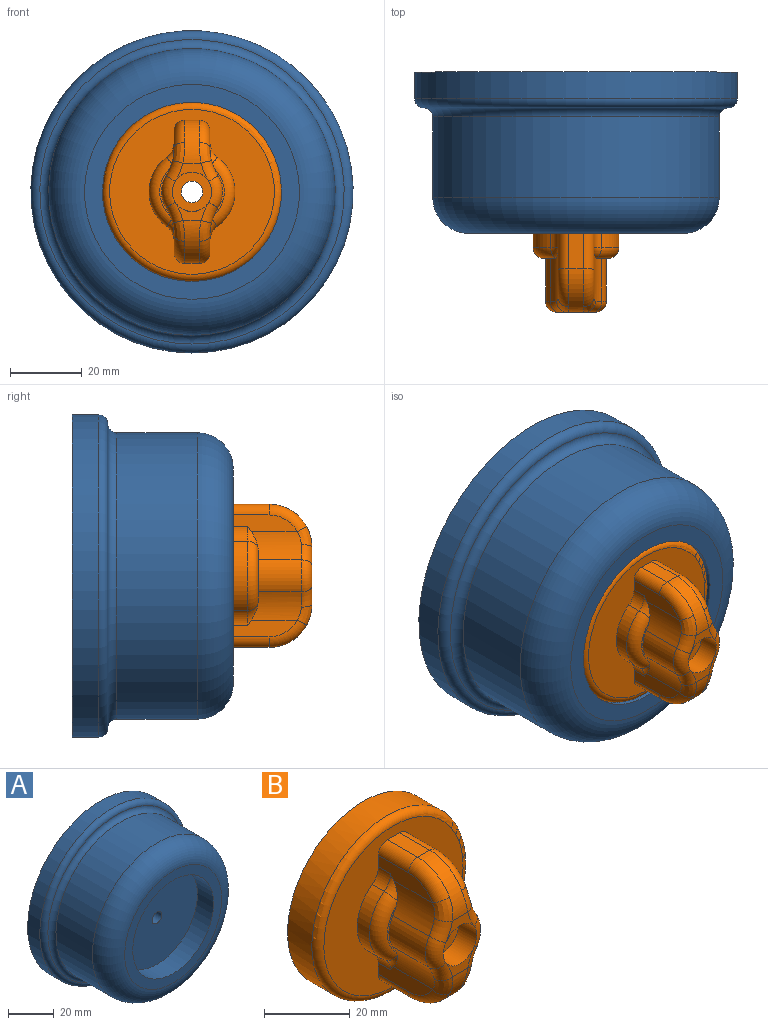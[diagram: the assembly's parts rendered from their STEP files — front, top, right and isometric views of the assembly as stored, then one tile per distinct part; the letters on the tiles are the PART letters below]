
ASSEMBLY  parts=2 mates=1
PART A: 10 faces, bbox 97.4x45x97.4 mm
  f0: cylinder r=3mm len=35mm, axis (0,-1,0), area 659.7mm2, adj f1,f9
  f1: plane 90x90mm, normal (0,1,0), area 6333.5mm2, adj f0,f2
  f2: cylinder r=45mm len=90mm, axis (0,-1,0), area 2120.6mm2, adj f1,f3
  f3: torus R=42.5mm, axis (0,-1,0), area 1087.9mm2, adj f2,f4
  f4: torus R=42.5mm, axis (0,-1,0), area 1009.4mm2, adj f3,f5
  f5: cylinder r=40mm len=80mm, axis (0,-1,0), area 5654.9mm2, adj f4,f6
  f6: torus R=30mm, axis (0,-1,0), area 3589.2mm2, adj f5,f7
  f7: plane 60x60mm, normal (0,-1,0), area 863.9mm2, adj f6,f8
  f8: cylinder r=25mm len=50mm, axis (0,-1,0), area 1570.8mm2, adj f7,f9
  f9: plane 50x50mm, normal (0,-1,0), area 1935.2mm2, adj f0,f8
PART B: 55 faces, bbox 54.1x32.1x54.1 mm
  f0: plane 9.36x5.11mm, normal (0,-1,0), area 18mm2, adj f30,f32,f44,f51
  f1: plane 17.9x4.68mm, normal (-1,0,0), area 66.4mm2, adj f2,f12,f19,f24,f37,f47
  f2: cylinder r=3mm len=10mm, axis (0,1,0), area 47.1mm2, adj f1,f3,f19,f47
  f3: plane 10x4mm, normal (0,0,-1), area 40mm2, adj f2,f4,f19,f33
  f4: cylinder r=3mm len=10mm, axis (0,1,0), area 47.1mm2, adj f3,f5,f19,f40
  f5: plane 17.9x4.68mm, normal (1,0,0), area 66.4mm2, adj f4,f13,f19,f25,f36,f40
  f6: plane 17.9x4.68mm, normal (1,0,0), area 66.4mm2, adj f7,f14,f19,f27,f34,f46
  f7: cylinder r=3mm len=10mm, axis (0,1,0), area 47.1mm2, adj f6,f8,f19,f46
  f8: plane 10x4mm, normal (0,0,1), area 40mm2, adj f7,f9,f19,f32
  f9: cylinder r=3mm len=10mm, axis (0,1,0), area 47.1mm2, adj f8,f10,f19,f53
  f10: plane 17.9x4.68mm, normal (-1,0,0), area 66.4mm2, adj f9,f11,f19,f22,f39,f53
  f11: cylinder r=15mm len=13.94mm, axis (0,1,0), area 101.9mm2, adj f10,f18,f28,f38,f39,f51,f52
  f12: cylinder r=15mm len=13.94mm, axis (0,1,0), area 101.9mm2, adj f1,f18,f28,f37,f38,f48,f49
  f13: cylinder r=15mm len=13.94mm, axis (0,1,0), area 101.9mm2, adj f5,f17,f29,f35,f36,f41,f42
  f14: cylinder r=15mm len=13.94mm, axis (0,1,0), area 101.9mm2, adj f6,f17,f29,f34,f35,f44,f45
  f15: plane 9.36x5.11mm, normal (0,-1,0), area 18mm2, adj f30,f33,f42,f49
  f16: cylinder r=3mm len=26mm, axis (0,-1,0), area 490.1mm2, adj f20,f31
  f17: plane 13.13x2.84mm, normal (0,-1,0), area 6.4mm2, adj f13,f14,f29,f35
  f18: plane 13.13x2.84mm, normal (0,-1,0), area 6.4mm2, adj f11,f12,f28,f38
  f19: plane 46x46mm, normal (0,-1,0), area 1045.5mm2, adj f1,f2,f3,f4,f5,f6,f7,f8
  f20: plane 50x50mm, normal (0,1,0), area 1935.2mm2, adj f16,f21
  f21: cylinder r=25mm len=50mm, axis (0,-1,0), area 1256.6mm2, adj f20,f54
  f22: cylinder r=5mm len=4.04mm, axis (0,1,0), area 18.8mm2, adj f10,f19,f23,f39
  f23: cylinder r=12mm len=19.41mm, axis (0,1,0), area 90.4mm2, adj f19,f22,f24,f38
  f24: cylinder r=5mm len=4.04mm, axis (0,1,0), area 18.8mm2, adj f1,f19,f23,f37
  f25: cylinder r=5mm len=4.04mm, axis (0,1,0), area 18.8mm2, adj f5,f19,f26,f36
  f26: cylinder r=12mm len=19.41mm, axis (0,1,0), area 90.4mm2, adj f19,f25,f27,f35
  f27: cylinder r=5mm len=4.04mm, axis (0,1,0), area 18.8mm2, adj f6,f19,f26,f34
  f28: cylinder r=8.5mm len=12mm, axis (0,1,0), area 112.8mm2, adj f11,f12,f18,f50
  f29: cylinder r=8.5mm len=12mm, axis (0,1,0), area 112.8mm2, adj f13,f14,f17,f43
  f30: cylinder r=5.5mm len=11mm, axis (0,-1,0), area 207.3mm2, adj f0,f15,f31,f43,f50
  f31: plane 11x11mm, normal (0,-1,0), area 66.8mm2, adj f16,f30
  f32: cylinder r=12mm len=12mm, axis (1,0,0), area 77.5mm2, adj f0,f8,f45,f46,f52,f53
  f33: cylinder r=12mm len=12mm, axis (1,0,0), area 77.5mm2, adj f3,f15,f40,f41,f47,f48
  f34: torus R=8mm, axis (0,-1,0), area 9.7mm2, adj f6,f14,f27,f35
  f35: torus R=9mm, axis (0,-1,0), area 96.1mm2, adj f13,f14,f17,f26,f34,f36
  f36: torus R=8mm, axis (0,-1,0), area 9.7mm2, adj f5,f13,f25,f35
  f37: torus R=8mm, axis (0,-1,0), area 9.7mm2, adj f1,f12,f24,f38
  f38: torus R=9mm, axis (0,-1,0), area 96.1mm2, adj f11,f12,f18,f23,f37,f39
  f39: torus R=8mm, axis (0,-1,0), area 9.7mm2, adj f10,f11,f22,f38
  f40: torus R=9mm, axis (1,0,0), area 54.9mm2, adj f4,f5,f33,f41
  f41: bspline ~10.63x5.3mm, area 23.6mm2, adj f13,f33,f40,f42
  f42: torus R=18mm, axis (0,-1,0), area 23.5mm2, adj f13,f15,f41,f43
  f43: torus R=5.5mm, axis (0,-1,0), area 38.6mm2, adj f29,f30,f42,f44
  f44: torus R=18mm, axis (0,-1,0), area 23.5mm2, adj f0,f14,f43,f45
  f45: bspline ~10.63x5.3mm, area 23.6mm2, adj f14,f32,f44,f46
  f46: torus R=9mm, axis (1,0,0), area 54.9mm2, adj f6,f7,f32,f45
  f47: torus R=9mm, axis (1,0,0), area 54.9mm2, adj f1,f2,f33,f48
  f48: bspline ~10.63x5.3mm, area 23.6mm2, adj f12,f33,f47,f49
  f49: torus R=18mm, axis (0,-1,0), area 23.5mm2, adj f12,f15,f48,f50
  f50: torus R=5.5mm, axis (0,-1,0), area 38.6mm2, adj f28,f30,f49,f51
  f51: torus R=18mm, axis (0,-1,0), area 23.5mm2, adj f0,f11,f50,f52
  f52: bspline ~10.63x5.3mm, area 23.6mm2, adj f11,f32,f51,f53
  f53: torus R=9mm, axis (1,0,0), area 54.9mm2, adj f9,f10,f32,f52
  f54: torus R=23mm, axis (0,1,0), area 479.1mm2, adj f19,f21
PLACE A at identity fixed
PLACE B rot(axis=(0,-1,0),0deg) t=(0,-35,0)mm
MATE revolute A.f0 <-> B.f16  axis (0,-1,0) through (0,-35,0)mm
